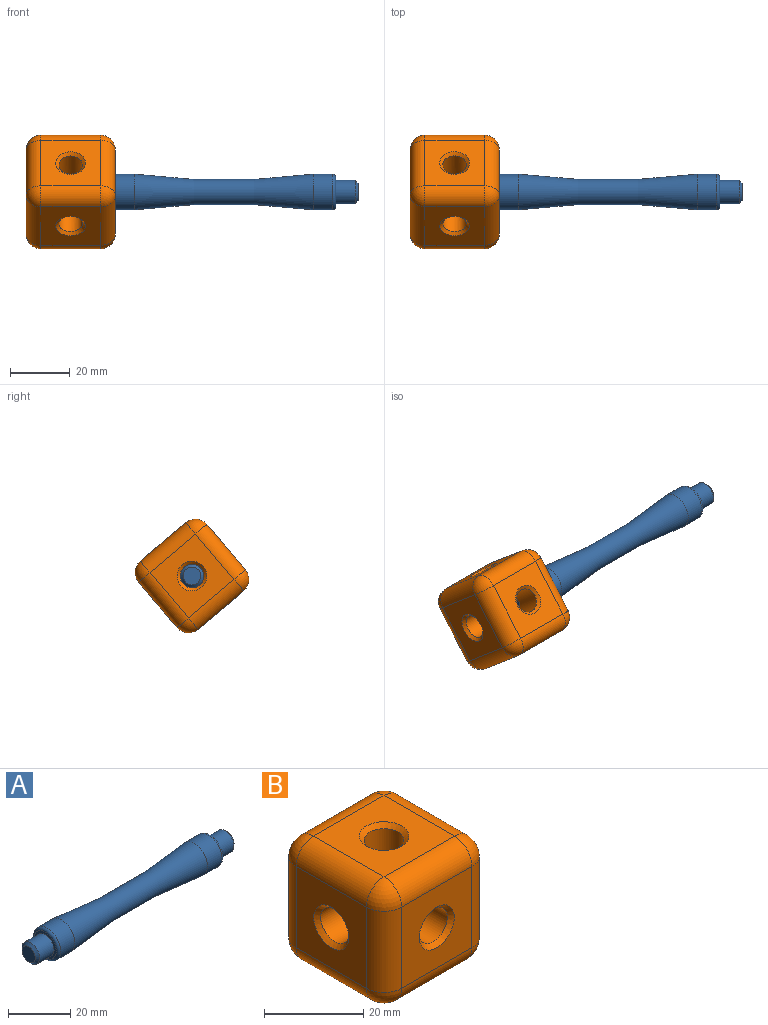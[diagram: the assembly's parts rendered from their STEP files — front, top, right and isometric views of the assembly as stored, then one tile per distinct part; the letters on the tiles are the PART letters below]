
ASSEMBLY  parts=2 mates=1
PART A: 13 faces, bbox 320.9x150.5x150.5 mm
  f0: plane 6x6mm, normal (-1,0,0), area 28.3mm2, adj f10
  f1: plane 6x6mm, normal (1,0,0), area 28.3mm2, adj f9
  f2: cylinder r=4mm len=8mm, axis (-1,0,0), area 163.4mm2, adj f3,f9
  f3: plane 10x10mm, normal (1,0,0), area 28.3mm2, adj f2,f11
  f4: cylinder r=6mm len=12mm, axis (-1,0,0), area 245mm2, adj f5,f11
  f5: torus R=230mm, axis (-1,0,0), area 1764.6mm2, adj f4,f6
  f6: cylinder r=6mm len=12mm, axis (-1,0,0), area 245mm2, adj f5,f12
  f7: plane 10x10mm, normal (-1,0,0), area 28.3mm2, adj f8,f12
  f8: cylinder r=4mm len=8mm, axis (-1,0,0), area 163.4mm2, adj f7,f10
  f9: cone r=4mm half-angle=45deg, axis (-1,0,0), area 31.1mm2, adj f1,f2
  f10: cone r=3mm half-angle=45deg, axis (1,0,0), area 31.1mm2, adj f0,f8
  f11: torus R=5mm, axis (-1,0,0), area 55.6mm2, adj f3,f4
  f12: torus R=5mm, axis (-1,0,0), area 55.6mm2, adj f6,f7
PART B: 38 faces, bbox 30x30x30 mm
  f0: cylinder r=4mm len=11.17mm, axis (0,-1,0), area 261.3mm2, adj f2,f3,f10,f11,f37
  f1: cylinder r=4mm len=11.17mm, axis (0,-1,0), area 261.3mm2, adj f2,f3,f10,f11,f35
  f2: cylinder r=4mm len=11.17mm, axis (-1,0,0), area 261.3mm2, adj f0,f1,f10,f11,f32
  f3: cylinder r=4mm len=11.17mm, axis (-1,0,0), area 261.3mm2, adj f0,f1,f10,f11,f33
  f4: plane 20x20mm, normal (1,0,0), area 321.5mm2, adj f20,f25,f28,f31,f32
  f5: plane 20x20mm, normal (0,0,1), area 321.5mm2, adj f17,f26,f27,f31,f34
  f6: plane 20x20mm, normal (-1,0,0), area 321.5mm2, adj f12,f16,f17,f18,f33
  f7: plane 20x20mm, normal (0,0,-1), area 321.5mm2, adj f12,f15,f19,f20,f36
  f8: plane 20x20mm, normal (0,-1,0), area 321.5mm2, adj f15,f16,f25,f26,f35
  f9: plane 20x20mm, normal (0,1,0), area 321.5mm2, adj f18,f19,f27,f28,f37
  f10: cylinder r=4mm len=11.17mm, axis (0,0,1), area 261.3mm2, adj f0,f1,f2,f3,f34
  f11: cylinder r=4mm len=11.17mm, axis (0,0,1), area 261.3mm2, adj f0,f1,f2,f3,f36
  f12: cylinder r=5mm len=20mm, axis (0,-1,0), area 157.1mm2, adj f6,f7,f13,f14
  f13: sphere r=5mm, area 39.3mm2, adj f12,f15,f16
  f14: sphere r=5mm, area 39.3mm2, adj f12,f18,f19
  f15: cylinder r=5mm len=20mm, axis (-1,0,0), area 157.1mm2, adj f7,f8,f13,f21
  f16: cylinder r=5mm len=20mm, axis (0,0,1), area 157.1mm2, adj f6,f8,f13,f22
  f17: cylinder r=5mm len=20mm, axis (0,1,0), area 157.1mm2, adj f5,f6,f22,f23
  f18: cylinder r=5mm len=20mm, axis (0,0,-1), area 157.1mm2, adj f6,f9,f14,f23
  f19: cylinder r=5mm len=20mm, axis (1,0,0), area 157.1mm2, adj f7,f9,f14,f24
  f20: cylinder r=5mm len=20mm, axis (0,1,0), area 157.1mm2, adj f4,f7,f21,f24
  f21: sphere r=5mm, area 39.3mm2, adj f15,f20,f25
  f22: sphere r=5mm, area 39.3mm2, adj f16,f17,f26
  f23: sphere r=5mm, area 39.3mm2, adj f17,f18,f27
  f24: sphere r=5mm, area 39.3mm2, adj f19,f20,f28
  f25: cylinder r=5mm len=20mm, axis (0,0,-1), area 157.1mm2, adj f4,f8,f21,f29
  f26: cylinder r=5mm len=20mm, axis (1,0,0), area 157.1mm2, adj f5,f8,f22,f29
  f27: cylinder r=5mm len=20mm, axis (-1,0,0), area 157.1mm2, adj f5,f9,f23,f30
  f28: cylinder r=5mm len=20mm, axis (0,0,1), area 157.1mm2, adj f4,f9,f24,f30
  f29: sphere r=5mm, area 39.3mm2, adj f25,f26,f31
  f30: sphere r=5mm, area 39.3mm2, adj f27,f28,f31
  f31: cylinder r=5mm len=20mm, axis (0,-1,0), area 157.1mm2, adj f4,f5,f29,f30
  f32: cone r=5mm half-angle=45deg, axis (1,0,0), area 40mm2, adj f2,f4
  f33: cone r=4mm half-angle=45deg, axis (-1,0,0), area 40mm2, adj f3,f6
  f34: cone r=4mm half-angle=45deg, axis (0,0,1), area 40mm2, adj f5,f10
  f35: cone r=4mm half-angle=45deg, axis (0,-1,0), area 40mm2, adj f1,f8
  f36: cone r=5mm half-angle=45deg, axis (0,0,-1), area 40mm2, adj f7,f11
  f37: cone r=5mm half-angle=45deg, axis (0,1,0), area 40mm2, adj f0,f9
PLACE A rot(axis=(0,-1,0),180deg) t=(-61.84,11.32,-2.42)mm fixed
PLACE B rot(axis=(1,0,0),139.7deg) t=(-8.34,11.32,-2.42)mm
MATE revolute A.f2 <-> B.f32  axis (-1,0,0) through (5.66,11.32,-2.42)mm
